# Revit family: ORIZ 5.125'' 2-6-SSD-Door-All
name_source: partatom
category: Mechanical Equipment
units: mm (PartAtom-declared; Revit-internal decimal feet)

## family parameters
Always vertical = Yes
Cut with Voids When Loaded = No
OmniClass Number = 23.40.40.11.17
OmniClass Title = Refrigerated Cases
Part Type = Normal
Room Calculation Point = No
Round Connector Dimension = Use Radius
Shared = No
Work Plane-Based = Yes

## types (3) — shared parameters
22" Shelf = Yes
Application Discipline = Frozen
BTUH Conventional = 855
BTUH Parallel = 831
Certifications = NSF 7, UL471, CSA
Combined Heated Rails Watts = 0 W
DATE = 02/10/2016
DRAIN LINE CONNECTION = SANITARY LINE CONNECTION
DRAIN LINE DIAMETER = 2"
DRAIN PIPE TYPE = PVC
DRIP PAN PLUMB TYPE = HARD
Default Elevation = 48"
Defrosts Per Day_2 = 1
Description = Back-to-Back Reach-In Glass Door Merchandiser
Discharge Air (°F) = -1° F
Discharge Air Velocity (FPM) = 350 (FPM)
EQUIPMENT DESCRIPTION = Back-to-Back Reach-In Glass Door Merchandiser
EQUIPMENT MARK = ORIZ
Electric Defrost Fail-Safe = 46 (Min)
Electric Defrost Run-Off Time (Min) = 0 (Min)
Electric Defrost Termination Temp (°F) = 50 °F
Evaporator (°F) = -7° F
GLASS = Glass
Heated/Low E = Heated
Height = 81 1/4"
Hot Gas Defrost Fail-Safe = 24 (Min)
Hot Gas Defrost Run-Off Time (Min) = 13-15 (Min)
Hot Gas Defrost Termination = 73° F
Individual Circuits Heated Doors Watts = 0"
Item Description = Back-to-Back Reach-In Glass Door Merchandiser
LIQUID LINE CONNECTION = LIQUID LINE CONNECTION
LIQUID LINE DIAMETER = 0"
LIQUID LINE RADIUS = 0"
Legend Number = ORIZ
Manufacturer = HILL PHOENIX
Model = ORIZ
NUMBER FOR GUIDLINES AND CONTROL ORGANIZATION = 2
PAINTED METAL UPPER SHELF = PAINTED SHELVES
PRESSURE REGULATOR = 0.00 psi
REFRIGERATION PIPING = COPPER PIPE
SANITARY PIPE SIZE = 1"
SUCTION LINE CONNECTION = SUCTION LINE CONNECTION
SUCTION LINE DIAMETER = 1"
SUCTION LINE RADIUS = 0"
Size of Door = 30"
Superheat Set Point @ Bulb (°F) = 3-5° F
URL = http://www.hillphoenix.com
Width = 67 1/8"

## per-type parameters (varying)
- SSD 6-Door-Frozen-Heated: # of door=3; CENTER LINE & DRAIN=90"; Combined Low E Rails Amps=4 A; Combined Low E Rails Watts=491 W; DOOR CONFIGURATION=MASTER DOOR : 30" X 64 3/8" 6 DOOR A SWING (LEFT OPENING); DRAIN HEATER AMPS=3 A; DRAIN HEATER WATTS=320 W; Defrost (Phase 1) 208 V Amps=20 A; Defrost (Phase 1) 208 V Watts=4224 W; Defrost (Phase 1) 240 V Amps=23 A; Defrost (Phase 1) 240 V Watts=5624 W; Defrost (Phase 3) 208 V Amps=18 A; Defrost (Phase 3) 208 V Watts=4224 W; Defrost (Phase 3) 240 V Amps=20 A; Defrost (Phase 3) 240 V Watts=5624 W; GE Immersion Amps=1 A; GE Immersion Watts=96 W; Heated Option (IG and Rails) Amps=5 A; Heated Option (IG and Rails) Watts=565 W; High Efficiency Amps=2 A; High Efficiency Watts=150 W; Individual 101-LE Frame Amps=3 A; Individual 101-LE Frame Watts=376 W; Individual Circuits Heated Doors Amps=2 A; Individual Low E Doors Amps=1 A; Individual Low E Doors Watts=115 W; Length=180"; Length of Cases=180"; NUMBER FOR ELECTRICAL DATA=10; Number of Fans=6; Optimax Pro Amps=0 A; Optimax Pro Watts=43 W; SSD Combined Heated Rails Amps=5 A; SSD Combined Heated Rails Watts=565 W; SSD Combined Low E Rails Amps=4 A; SSD Combined Low E Rails Watts=491 W; SSD Defrost (Phase 1) 208 V Amps=20 A; SSD Defrost (Phase 1) 208 V Watts=4224 W; SSD Defrost (Phase 1) 240 V Amps=23 A; SSD Defrost (Phase 1) 240 V Watts=5624 W; SSD Defrost (Phase 3) 208 V Amps=18 A; SSD Defrost (Phase 3) 208 V Watts=4224 W; SSD Defrost (Phase 3) 240 V Amps=20 A; SSD Defrost (Phase 3) 240 V Watts=5624 W; SSD Fans Per Case=6; SSD GE Immersion Amps=1 A; SSD GE Immersion Watts=96 W; SSD High Efficiency Amps=2 A; SSD High Efficiency Watts=150 W; SSD Individual 101-LE Frame Amps=3 A; SSD Individual 101-LE Frame Watts=376 W; SSD Individual Heated Doors Amps=2 A; SSD Individual Heated Doors Watts=190 W; SSD Individual Low E Doors Amps=1 A; SSD Individual Low E Doors Watts=115 W; SSD Optimax Pro Amps=1 A; SSD Optimax Pro Watts=115 W; SSD Tank/Drain Heater Amps=3 A; SSD Tank/Drain Heater Watts=320 W
- SSD 4-Door-Frozen-Heated: # of door=4; CENTER LINE & DRAIN=60"; Combined Low E Rails Amps=3 A; Combined Low E Rails Watts=338 W; DOOR CONFIGURATION=MASTER DOOR : 30" X 64 3/8" 4 DOOR A SWING (LEFT OPENING); DRAIN HEATER AMPS=2 A; DRAIN HEATER WATTS=226 W; Defrost (Phase 1) 208 V Amps=14 A; Defrost (Phase 1) 208 V Watts=2984 W; Defrost (Phase 1) 240 V Amps=17 A; Defrost (Phase 1) 240 V Watts=3992 W; Defrost (Phase 3) 208 V Amps=12 A; Defrost (Phase 3) 208 V Watts=2984 W; Defrost (Phase 3) 240 V Amps=14 A; Defrost (Phase 3) 240 V Watts=3992 W; GE Immersion Amps=1 A; GE Immersion Watts=64 W; Heated Option (IG and Rails) Amps=4 A; Heated Option (IG and Rails) Watts=388 W; High Efficiency Amps=1 A; High Efficiency Watts=100 W; Individual 101-LE Frame Amps=2 A; Individual 101-LE Frame Watts=262 W; Individual Circuits Heated Doors Amps=1 A; Individual Low E Doors Amps=1 A; Individual Low E Doors Watts=77 W; Length=120"; Length of Cases=120"; NUMBER FOR ELECTRICAL DATA=8; Number of Fans=4; Optimax Pro Amps=1 A; Optimax Pro Watts=65 W; SSD Combined Heated Rails Amps=4 A; SSD Combined Heated Rails Watts=388 W; SSD Combined Low E Rails Amps=3 A; SSD Combined Low E Rails Watts=338 W; SSD Defrost (Phase 1) 208 V Amps=14 A; SSD Defrost (Phase 1) 208 V Watts=2984 W; SSD Defrost (Phase 1) 240 V Amps=17 A; SSD Defrost (Phase 1) 240 V Watts=3992 W; SSD Defrost (Phase 3) 208 V Amps=12040 A; SSD Defrost (Phase 3) 208 V Watts=2984 W; SSD Defrost (Phase 3) 240 V Amps=14 A; SSD Defrost (Phase 3) 240 V Watts=3992 W; SSD Fans Per Case=4; SSD GE Immersion Amps=0 A; SSD GE Immersion Watts=64 W; SSD High Efficiency Amps=1 A; SSD High Efficiency Watts=100 W; SSD Individual 101-LE Frame Amps=2 A; SSD Individual 101-LE Frame Watts=262 W; SSD Individual Heated Doors Amps=1 A; SSD Individual Heated Doors Watts=126 W; SSD Individual Low E Doors Amps=1 A; SSD Individual Low E Doors Watts=77 W; SSD Optimax Pro Amps=1 A; SSD Optimax Pro Watts=77 W; SSD Tank/Drain Heater Amps=2 A; SSD Tank/Drain Heater Watts=226 W
- SSD 2-Door-Frozen-Heated: # of door=2; CENTER LINE & DRAIN=30"; Combined Low E Rails Amps=2 A; Combined Low E Rails Watts=181 W; DOOR CONFIGURATION=MASTER DOOR : 30" X 64 3/8" 2 DOOR B SWING; DRAIN HEATER AMPS=1 A; DRAIN HEATER WATTS=152 W; Defrost (Phase 1) 208 V Amps=8 A; Defrost (Phase 1) 208 V Watts=1552 W; Defrost (Phase 1) 240 V Amps=9 A; Defrost (Phase 1) 240 V Watts=2068 W; Defrost (Phase 3) 208 V Amps=7 A; Defrost (Phase 3) 208 V Watts=1552 W; Defrost (Phase 3) 240 V Amps=8 A; Defrost (Phase 3) 240 V Watts=2068 W; GE Immersion Amps=0 A; GE Immersion Watts=32 W; Heated Option (IG and Rails) Amps=2 A; Heated Option (IG and Rails) Watts=206 W; High Efficiency Amps=1 A; High Efficiency Watts=50 W; Individual 101-LE Frame Amps=1 A; Individual 101-LE Frame Watts=143 W; Individual Circuits Heated Doors Amps=1 A; Individual Low E Doors Amps=0 A; Individual Low E Doors Watts=38 W; Length=60"; Length of Cases=60"; NUMBER FOR ELECTRICAL DATA=6; Number of Fans=2; Optimax Pro Amps=0 A; Optimax Pro Watts=39 W; SSD Combined Heated Rails Amps=2 A; SSD Combined Heated Rails Watts=206 W; SSD Combined Low E Rails Amps=2 A; SSD Combined Low E Rails Watts=181 W; SSD Defrost (Phase 1) 208 V Amps=8 A; SSD Defrost (Phase 1) 208 V Watts=1552 W; SSD Defrost (Phase 1) 240 V Amps=9 A; SSD Defrost (Phase 1) 240 V Watts=2068 W; SSD Defrost (Phase 3) 208 V Amps=7 A; SSD Defrost (Phase 3) 208 V Watts=1552 W; SSD Defrost (Phase 3) 240 V Amps=8 A; SSD Defrost (Phase 3) 240 V Watts=2068 W; SSD Fans Per Case=2; SSD GE Immersion Amps=0 A; SSD GE Immersion Watts=32 W; SSD High Efficiency Amps=1 A; SSD High Efficiency Watts=50 W; SSD Individual 101-LE Frame Amps=1 A; SSD Individual 101-LE Frame Watts=143 W; SSD Individual Heated Doors Amps=1 A; SSD Individual Heated Doors Watts=63 W; SSD Individual Low E Doors Amps=0 A; SSD Individual Low E Doors Watts=38 W; SSD Optimax Pro Amps=0 A; SSD Optimax Pro Watts=39 W; SSD Tank/Drain Heater Amps=1 A; SSD Tank/Drain Heater Watts=152 W

## geometry (parser evidence)
native form markers: Blend x8, Sweep x38
no freeform markers — native parametric forms only
